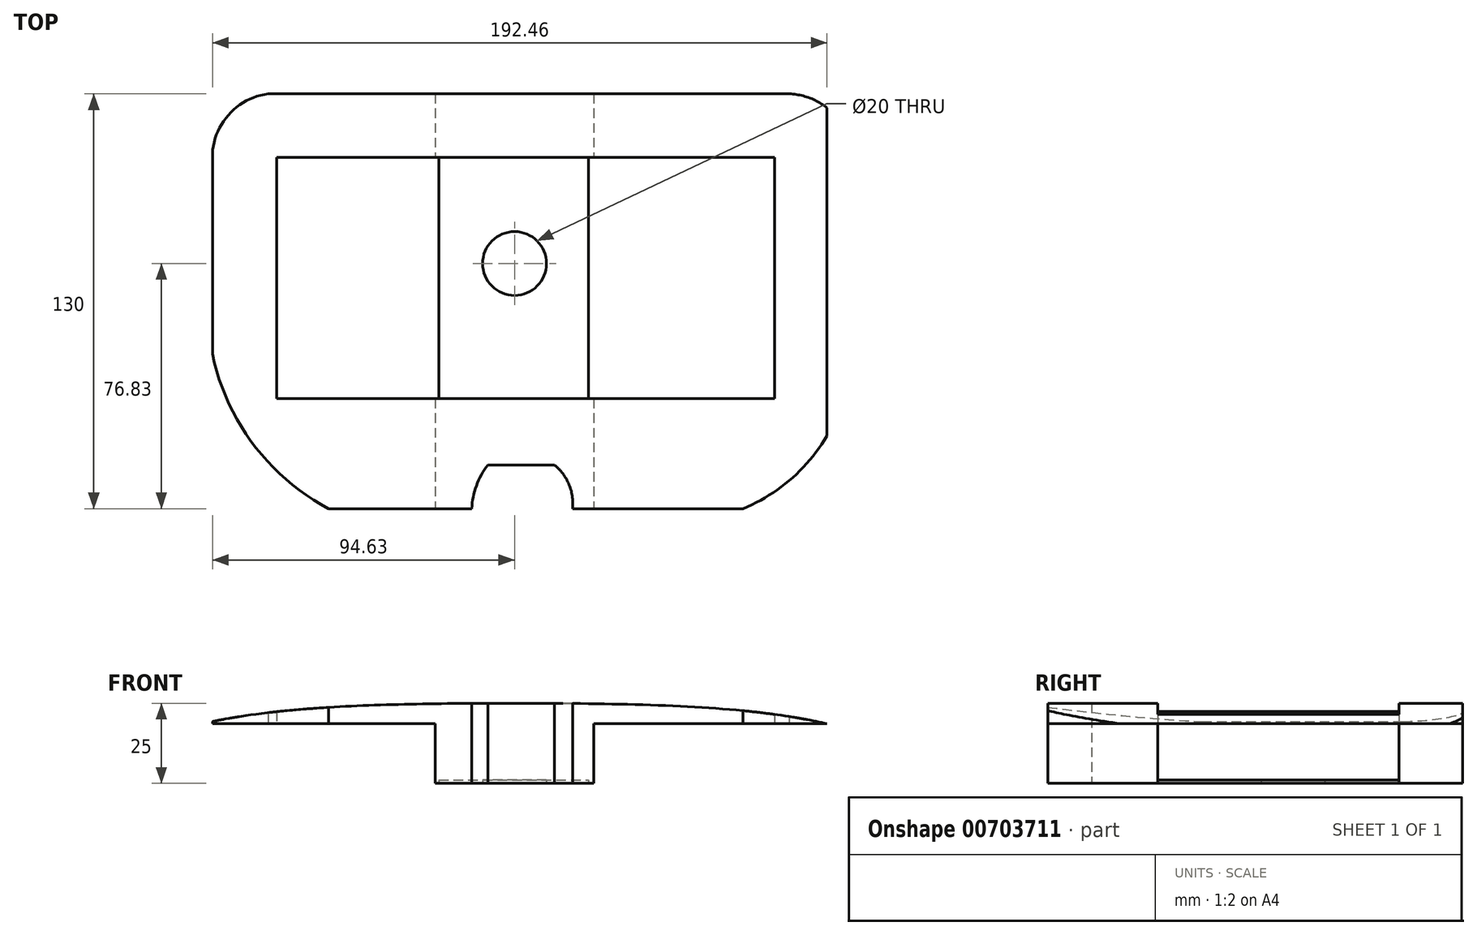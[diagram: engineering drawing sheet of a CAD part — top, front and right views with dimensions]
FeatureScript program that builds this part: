
annotation { "Feature Type Name" : "Feature", "Feature Type Description" : "" }
export const myFeature = defineFeature(function(context is Context, id is Id, definition is map)
    precondition{}
    {
        {
            var Q0;
            Q0=qCreatedBy(makeId("Top.planeOp"),FACE);
            var sketch = newSketch(context, id + "F0", { "sketchPlane" : qUnion([Q0])});
            skLineSegment(sketch, "E0.bottom", {"start": v(-94.63, 53.17) * mm, "end": v(105.37, 53.17) * mm});
            skLineSegment(sketch, "E0.top", {"start": v(-94.63, -76.83) * mm, "end": v(105.37, -76.83) * mm});
            skLineSegment(sketch, "E0.left", {"start": v(-94.63, 53.17) * mm, "end": v(-94.63, -76.83) * mm});
            skLineSegment(sketch, "E0.right", {"start": v(105.37, 53.17) * mm, "end": v(105.37, -76.83) * mm});
            skArc(sketch, "E1", {"start": v(-94.63, -28.4) * mm, "mid": v(-81.8, -56.66) * mm, "end": v(-58.23, -76.83) * mm});
            skArc(sketch, "E2", {"start": v(71.49, -76.83) * mm, "mid": v(95.53, -57.59) * mm, "end": v(105.37, -28.4) * mm});
            skArc(sketch, "E3", {"start": v(-77.17, 53.17) * mm, "mid": v(-89.28, 46.93) * mm, "end": v(-94.63, 34.4) * mm});
            skArc(sketch, "E4", {"start": v(105.37, 35.03) * mm, "mid": v(98.49, 48.25) * mm, "end": v(84.43, 53.17) * mm});
            skArc(sketch, "E5", {"start": v(-8.36, -63.1) * mm, "mid": v(-11.92, -69.59) * mm, "end": v(-13.41, -76.83) * mm});
            skLineSegment(sketch, "E6", {"start": v(-8.36, -63.1) * mm, "end": v(12.47, -63.1) * mm});
            skArc(sketch, "E7", {"start": v(18.15, -76.83) * mm, "mid": v(17.07, -69.24) * mm, "end": v(12.47, -63.1) * mm});
            skLineSegment(sketch, "E8.bottom", {"start": v(-74.55, 33.22) * mm, "end": v(81.45, 33.22) * mm});
            skLineSegment(sketch, "E8.top", {"start": v(-74.55, -42.33) * mm, "end": v(81.45, -42.33) * mm});
            skLineSegment(sketch, "E8.left", {"start": v(-74.55, 33.22) * mm, "end": v(-74.55, -42.33) * mm});
            skLineSegment(sketch, "E8.right", {"start": v(81.45, 33.22) * mm, "end": v(81.45, -42.33) * mm});
            skSolve(sketch);
        }
        {
            var Q0;
            {var subQ1=sQuery(id+"F0.wireOp",EDGE,"E1");Q0=makeQuery(id+"F0.imprint","IMPRINT",FACE,{"disambiguationData":[TD([[makeQuery(id+"F0.imprint","IMPRINT",EDGE,{"derivedFrom":subQ1}),1.0]])]});}
            extrude(context, id + "F1", {"entities" : qUnion([Q0]), "depth" : 25 * mm, "offsetDistance" : 25 * mm});
        }
        {
            var Q0;
            Q0=qCreatedBy(makeId("Top.planeOp"),FACE);
            var sketch = newSketch(context, id + "F2", { "sketchPlane" : qUnion([Q0])});
            skLineSegment(sketch, "E9.bottom", {"start": v(-23.72, 33.36) * mm, "end": v(23.13, 33.36) * mm});
            skLineSegment(sketch, "E9.top", {"start": v(-23.72, -42.42) * mm, "end": v(23.13, -42.42) * mm});
            skLineSegment(sketch, "E9.left", {"start": v(-23.72, 33.36) * mm, "end": v(-23.72, -42.42) * mm});
            skLineSegment(sketch, "E9.right", {"start": v(23.13, 33.36) * mm, "end": v(23.13, -42.42) * mm});
            skSolve(sketch);
        }
        {
            var Q0;
            Q0=makeQuery(id+"F2.imprint","IMPRINT",FACE,{"disambiguationData":[TD([[makeQuery(id+"F2.imprint","IMPRINT",EDGE,{"derivedFrom":sQuery(id+"F2.wireOp",EDGE,"E9.bottom")}),-1.0]])]});
            extrude(context, id + "F3", {"entities" : qUnion([Q0]), "operationType" : NewBodyOperationType.ADD, "depth" : 1 * mm, "offsetDistance" : 25 * mm});
        }
        {
            var Q0;
            Q0=qCreatedBy(makeId("Top.planeOp"),FACE);
            var sketch = newSketch(context, id + "F4", { "sketchPlane" : qUnion([Q0])});
            skCircle(sketch, "E10", {"center": v(0, 0) * mm, "radius": 10.14 * mm});
            skSolve(sketch);
        }
        {
            var Q0;
            Q0=sQuery(id+"F4.wireOp",VERTEX,"E10.center");
            var Q1;
            Q1=makeQuery(id+"F1.opExtrude","SWEPT_BODY",BODY,{"disambiguationData":[OSD([sQuery(id+"F0.wireOp",EDGE,"E0.bottom"),sQuery(id+"F0.wireOp",EDGE,"E0.top"),sQuery(id+"F0.wireOp",EDGE,"E0.left"),sQuery(id+"F0.wireOp",EDGE,"E0.right"),sQuery(id+"F0.wireOp",EDGE,"E1"),sQuery(id+"F0.wireOp",EDGE,"E2"),sQuery(id+"F0.wireOp",EDGE,"E3"),sQuery(id+"F0.wireOp",EDGE,"E4"),sQuery(id+"F0.wireOp",EDGE,"E5"),sQuery(id+"F0.wireOp",EDGE,"E6"),sQuery(id+"F0.wireOp",EDGE,"E7"),sQuery(id+"F0.wireOp",EDGE,"E8.bottom"),sQuery(id+"F0.wireOp",EDGE,"E8.top"),sQuery(id+"F0.wireOp",EDGE,"E8.left"),sQuery(id+"F0.wireOp",EDGE,"E8.right")])]});
            hole(context, id + "F5", {"style" : HoleStyle.SIMPLE, "endStyle" : HoleEndStyle.THROUGH, "oppositeDirection" : true, "holeDiameter" : 20 * mm, "majorDiameter" : 5 * mm, "isTappedThrough" : true, "tappedDepth" : 12 * mm, "tapClearance" : 3, "startFromSketch" : true, "locations" : qUnion([Q0]), "scope" : qUnion([Q1])});
        }
        {
            var Q0;
            Q0=makeQuery(id+"F1.opExtrude","SWEPT_FACE",FACE,{"disambiguationData":[OSD([sQuery(id+"F0.wireOp",EDGE,"E0.bottom")])]});
            var sketch = newSketch(context, id + "F6", { "sketchPlane" : qUnion([Q0])});
            skFitSpline(sketch, "E11", {"points": [v(0, 25) * mm, v(74.94, 22.37) * mm, v(107.89, 15.53) * mm], "startDerivative": vector(134.46, 0.6) * mm, "endDerivative": vector(53.94, -21.6) * mm});
            skLineSegment(sketch, "E12", {"start": v(107.89, 15.53) * mm, "end": v(107.89, 28.55) * mm});
            skLineSegment(sketch, "E13", {"start": v(107.89, 28.55) * mm, "end": v(20.45, 28.55) * mm});
            skLineSegment(sketch, "E14", {"start": v(20.45, 28.55) * mm, "end": v(0, 25) * mm});
            skLineSegment(sketch, "E15.MirrorCS", {"start": v(-20.45, 28.55) * mm, "end": v(0, 25) * mm});
            skLineSegment(sketch, "E16.MirrorCS", {"start": v(-107.89, 28.55) * mm, "end": v(-20.45, 28.55) * mm});
            skFitSpline(sketch, "E17.MirrorCS", {"points": [v(0, 25) * mm, v(-74.94, 22.37) * mm, v(-107.89, 15.53) * mm], "startDerivative": vector(-134.46, 0.6) * mm, "endDerivative": vector(-53.94, -21.6) * mm});
            skLineSegment(sketch, "E18.MirrorCS", {"start": v(-107.89, 15.53) * mm, "end": v(-107.89, 28.55) * mm});
            skSolve(sketch);
        }
        {
            var Q0;
            Q0 = qSketchRegion(id + "F6", true);
            extrude(context, id + "F7", {"entities" : qUnion([Q0]), "operationType" : NewBodyOperationType.REMOVE, "oppositeDirection" : true, "depth" : 255 * mm, "offsetDistance" : 25 * mm});
        }
        {
            var Q0;
            Q0=qCreatedBy(makeId("Front.planeOp"),FACE);
            var sketch = newSketch(context, id + "F8", { "sketchPlane" : qUnion([Q0])});
            skLineSegment(sketch, "E19.bottom", {"start": v(-108.44, -14.11) * mm, "end": v(-24.8, -14.11) * mm});
            skLineSegment(sketch, "E19.top", {"start": v(-108.44, 18.6) * mm, "end": v(-24.8, 18.6) * mm});
            skLineSegment(sketch, "E19.left", {"start": v(-108.44, -14.11) * mm, "end": v(-108.44, 18.6) * mm});
            skLineSegment(sketch, "E19.right", {"start": v(-24.8, -14.11) * mm, "end": v(-24.8, 18.6) * mm});
            skLineSegment(sketch, "E20.MirrorCS", {"start": v(108.44, -14.11) * mm, "end": v(24.8, -14.11) * mm});
            skLineSegment(sketch, "E21.MirrorCS", {"start": v(24.8, -14.11) * mm, "end": v(24.8, 18.6) * mm});
            skLineSegment(sketch, "E22.MirrorCS", {"start": v(108.44, 18.6) * mm, "end": v(24.8, 18.6) * mm});
            skLineSegment(sketch, "E23.MirrorCS", {"start": v(108.44, -14.11) * mm, "end": v(108.44, 18.6) * mm});
            skSolve(sketch);
        }
        {
            var Q0;
            Q0=makeQuery(id+"F8.imprint","IMPRINT",FACE,{"disambiguationData":[TD([[makeQuery(id+"F8.imprint","IMPRINT",EDGE,{"derivedFrom":sQuery(id+"F8.wireOp",EDGE,"E19.bottom")}),1.0]])]});
            var Q1;
            Q1=makeQuery(id+"F8.imprint","IMPRINT",FACE,{"disambiguationData":[TD([[makeQuery(id+"F8.imprint","IMPRINT",EDGE,{"derivedFrom":sQuery(id+"F8.wireOp",EDGE,"E20.MirrorCS")}),-1.0]])]});
            extrude(context, id + "F9", {"entities" : qUnion([Q0, Q1]), "operationType" : NewBodyOperationType.REMOVE, "endBound" : BoundingType.SYMMETRIC, "depth" : 200 * mm, "offsetDistance" : 25 * mm});
        }
    });
